# Revit family: Building-Materials_Glass-Glazing_Vitro-Architectural-Glass_Optigray-Glass
name_source: partatom
category: Curtain Panels
units: mm (PartAtom-declared; Revit-internal decimal feet)

## family parameters
Always vertical = Yes
Classification Number = 23.25.20.14.11.11.17
Cut with Voids When Loaded = No
Shared = No

## types (11) — shared parameters
1st Lite Thickness = 0' - 0 1/4"
2nd Lite Thickness = 0' - 0 1/4"
Airspace Thickness = 0' - 0 1/2"
Analytic Construction = Low-E double glazing (1/4 in + 1/4 in)
Assembly Code = B2020220
Define Thermal Properties by = Schematic Type
Description = Optigray® glass is designed to eliminate the green cast typically found in conventional clear glass formulations. It produces a warm, ultra‑neutral aesthetic that brings crispness to vision glazing.
Finish = Glass
Heat Transfer Coefficient (U) = 0.29 BTU/(h·ft²·°F)
Keynote = 08900
Manufacturer = Vitro Architectural Glass
Product Guid = 87b7abbd-c069-453f-a496-ebe30e1be767
Product Page URL = https://www.vitroglazings.com
Product data url = https://www.bimobject.com
Thermal Resistance (R) = 8.3333 (h·ft²·°F)/BTU
Total Thickness = 0' - 1"
URL = https://www.vitroglazings.com

## per-type parameters (varying)
| type | Exterior Glass Material | Glass Code | ISO Damage Weighted Transmittance | Interior Glass Material | Light to Solar Gain | Reflectance (Visible Exterior) | Reflectance (Visible Interior) | Shadow Coefficient | Solar Heat Gain Coefficient | Solar Light Transmittance | U-Value Air (Summer Day) | U-Value Air (Winter Night) | U-Value Argon (Summer Day) | U-Value Argon (Winter Night) | UV Light Transmittance | Visual Light Transmittance |
| Optigray + Clear | Vitro Architectural-Glass - Optigray | 2 | 0.481 | Vitro Architectural-Glass - Clear | 1.08 | 10 | 13 | 0.6 | 0.52 | 0.41 | 0.5 BTU/(h·ft²·°F) | 0.47 BTU/(h·ft²·°F) | 0.48 BTU/(h·ft²·°F) | 0.45 BTU/(h·ft²·°F) | 0.27 | 0.56 |
| Optigray + Sungate 400 (3) Clear | Vitro Architectural-Glass - Optigray | 3 | 0.428 | Vitro Architectural-Glass - Sungate 400 (3) Clear | 1.17 | 9 | 12 | 0.52 | 0.46 | 0.34 | 0.31 BTU/(h·ft²·°F) | 0.32 BTU/(h·ft²·°F) | 0.26 BTU/(h·ft²·°F) | 0.28 BTU/(h·ft²·°F) | 0.16 | 0.54 |
| Solarban 60 (2) Optigray  + Clear | Vitro Architectural-Glass - Solarban 60 (2) Optigray | 4 | 0.375 | Vitro Architectural-Glass - Clear | 1.67 | 8 | 11 | 0.35 | 0.3 | 0.23 | 0.27 BTU/(h·ft²·°F) | 0.29 BTU/(h·ft²·°F) | 0.22 BTU/(h·ft²·°F) | 0.24 BTU/(h·ft²·°F) | 0.1 | 0.5 |
| Optigray + Solarban 60 (3) Clear | Vitro Architectural-Glass - Optigray | 5 | 0.375 | Vitro Architectural-Glass - Solarban 60 (3) Clear | 1.43 | 8 | 9 | 0.4 | 0.35 | 0.23 | 0.27 BTU/(h·ft²·°F) | 0.29 BTU/(h·ft²·°F) | 0.22 BTU/(h·ft²·°F) | 0.24 BTU/(h·ft²·°F) | 0.1 | 0.5 |
| Solarban 67 (2) Optigray  + Clear | Vitro Architectural-Glass - Solarban 67 (2) Optigray | 6 | 0.28 | Vitro Architectural-Glass - Clear | 1.58 | 12 | 15 | 0.27 | 0.24 | 0.17 | 0.27 BTU/(h·ft²·°F) | 0.29 BTU/(h·ft²·°F) | 0.22 BTU/(h·ft²·°F) | 0.24 BTU/(h·ft²·°F) | 0.06 | 0.38 |
| Optigray + Solarban 67 (3) Clear | Vitro Architectural-Glass - Optigray | 7 | 0.28 | Vitro Architectural-Glass - Solarban 67 (3) Clear | 1.19 | 10 | 18 | 0.36 | 0.32 | 0.17 | 0.27 BTU/(h·ft²·°F) | 0.29 BTU/(h·ft²·°F) | 0.22 BTU/(h·ft²·°F) | 0.24 BTU/(h·ft²·°F) | 0.06 | 0.38 |
| Solarban 70 (2) Optigray  + Clear | Vitro Architectural-Glass - Solarban 70 (2) Optigray | 8 | 0.306 | Vitro Architectural-Glass - Clear | 2 | 9 | 13 | 0.26 | 0.23 | 0.17 | 0.26 BTU/(h·ft²·°F) | 0.28 BTU/(h·ft²·°F) | 0.21 BTU/(h·ft²·°F) | 0.24 BTU/(h·ft²·°F) | 0.04 | 0.46 |
| Optigray + Solarban 70 (3) | Vitro Architectural-Glass - Optigray | 9 | 0.305 | Vitro Architectural-Glass - Solarban 70 (3) | 1.64 | 9 | 12 | 0.32 | 0.28 | 0.17 | 0.26 BTU/(h·ft²·°F) | 0.28 BTU/(h·ft²·°F) | 0.21 BTU/(h·ft²·°F) | 0.24 BTU/(h·ft²·°F) | 0.04 | 0.46 |
| Solarban R100 (2) Optigray + Clear | Vitro Architectural-Glass - Solarban R100 (2) Optigray | 10 | 0.234 | Vitro Architectural-Glass - Clear | 1.45 | 18 | 13 | 0.23 | 0.2 | 0.13 | 0.27 BTU/(h·ft²·°F) | 0.29 BTU/(h·ft²·°F) | 0.22 BTU/(h·ft²·°F) | 0.25 BTU/(h·ft²·°F) | 0.06 | 0.29 |
| Solarban 90 (2) Optigray  + Clear | Vitro Architectural-Glass - Solarban 90 (2) Optigray | 11 | 0.252 | Vitro Architectural-Glass - Clear | 1.8 | 8 | 19 | 0.23 | 0.2 | 0.13 | 0.27 BTU/(h·ft²·°F) | 0.29 BTU/(h·ft²·°F) | 0.21 BTU/(h·ft²·°F) | 0.24 BTU/(h·ft²·°F) | 0.04 | 0.36 |
| Optigray + Solarban 90 (3) Clear | Vitro Architectural-Glass - Optigray | 12 | 0.251 | Vitro Architectural-Glass - Solarban 90 (3) Clear | 1.33 | 12 | 11 | 0.31 | 0.27 | 0.13 | 0.27 BTU/(h·ft²·°F) | 0.29 BTU/(h·ft²·°F) | 0.21 BTU/(h·ft²·°F) | 0.24 BTU/(h·ft²·°F) | 0.04 | 0.36 |

note: column(s) folded — value = type name in every type: Model

## geometry (parser evidence)
native form markers: Sweep x1
no freeform markers — native parametric forms only
